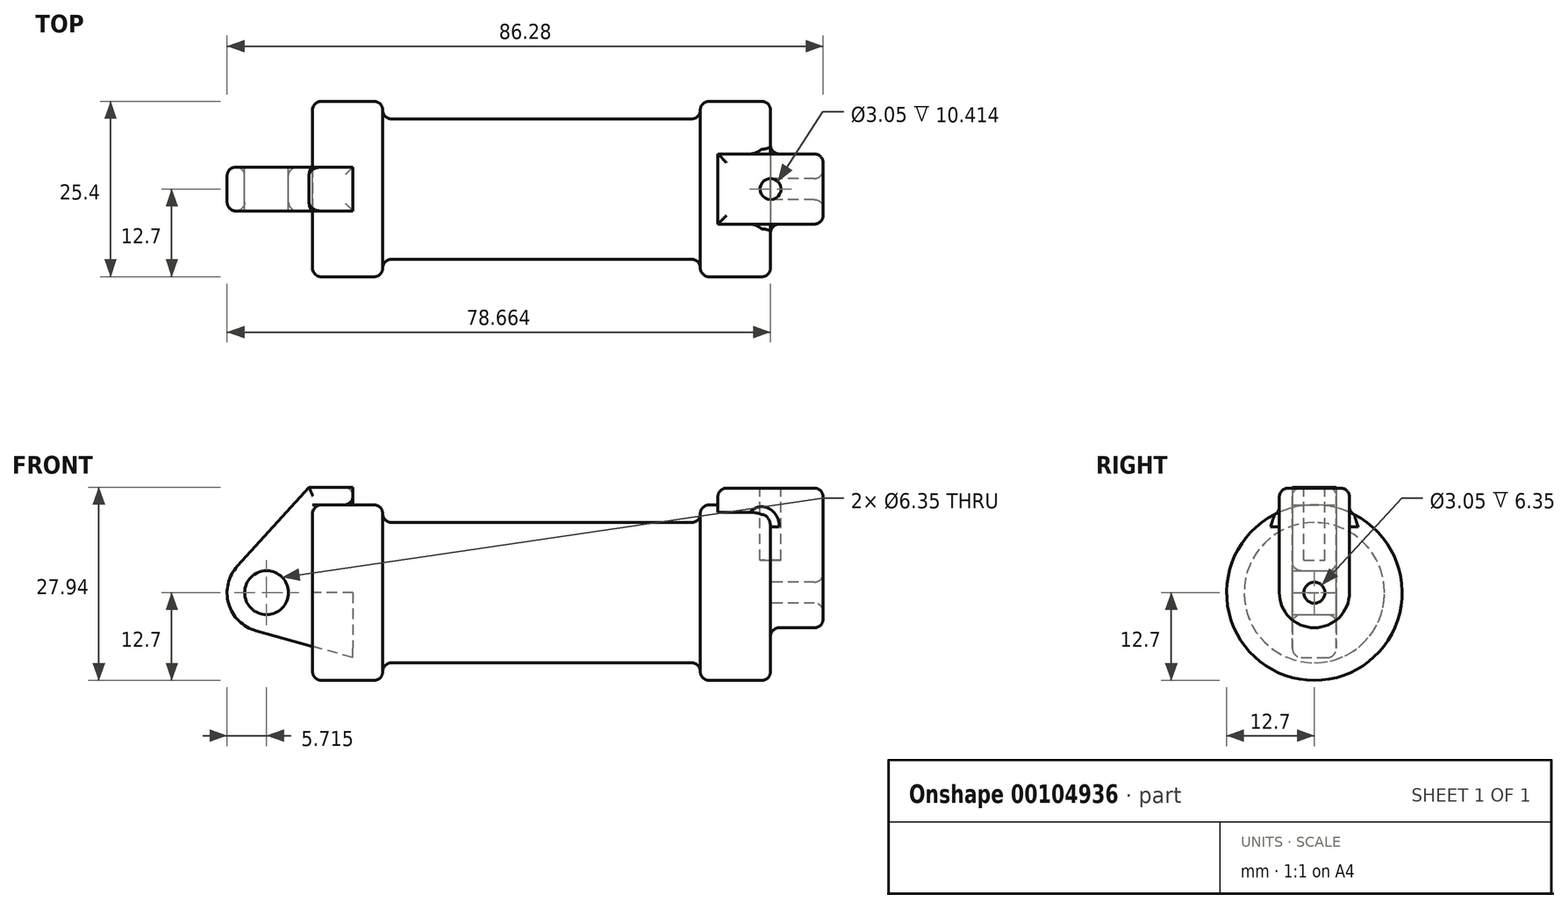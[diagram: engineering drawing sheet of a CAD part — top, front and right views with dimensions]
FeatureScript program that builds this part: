
annotation { "Feature Type Name" : "Feature", "Feature Type Description" : "" }
export const myFeature = defineFeature(function(context is Context, id is Id, definition is map)
    precondition{}
    {
        {
            var Q0;
            Q0=qCreatedBy(makeId("Front.planeOp"),FACE);
            var sketch = newSketch(context, id + "F0", { "sketchPlane" : qUnion([Q0])});
            skLineSegment(sketch, "E0", {"start": v(0, 0) * mm, "end": v(0, 12.7) * mm});
            skLineSegment(sketch, "E1", {"start": v(0, 12.7) * mm, "end": v(10.16, 12.7) * mm});
            skLineSegment(sketch, "E2", {"start": v(10.16, 12.7) * mm, "end": v(10.16, 10.16) * mm});
            skLineSegment(sketch, "E3", {"start": v(10.16, 10.16) * mm, "end": v(56.13, 10.16) * mm});
            skLineSegment(sketch, "E4", {"start": v(56.13, 10.16) * mm, "end": v(56.13, 12.7) * mm});
            skLineSegment(sketch, "E5", {"start": v(56.13, 12.7) * mm, "end": v(66.3, 12.7) * mm});
            skLineSegment(sketch, "E6", {"start": v(66.3, 12.7) * mm, "end": v(66.3, 0) * mm});
            skLineSegment(sketch, "E7", {"start": v(66.3, 0) * mm, "end": v(0, 0) * mm});
            skLineSegment(sketch, "E8", {"start": v(5.84, 15.24) * mm, "end": v(-0.5, 15.24) * mm});
            skLineSegment(sketch, "E9", {"start": v(-0.5, 15.24) * mm, "end": v(-10.88, 3.85) * mm});
            skLineSegment(sketch, "E10", {"start": v(0, 0) * mm, "end": v(-6.65, 0) * mm});
            skCircle(sketch, "E11", {"center": v(-6.65, 0) * mm, "radius": 5.72 * mm});
            skCircle(sketch, "E12", {"center": v(-6.65, 0) * mm, "radius": 3.18 * mm});
            skLineSegment(sketch, "E13", {"start": v(5.84, 15.24) * mm, "end": v(5.84, -9.4) * mm});
            skLineSegment(sketch, "E14", {"start": v(5.84, -9.4) * mm, "end": v(-8.18, -5.5) * mm});
            skSolve(sketch);
        }
        {
            var Q0;
            {var subQ0=sQuery(id+"F0.wireOp",EDGE,"E2");Q0=makeQuery(id+"F0.imprint","IMPRINT",FACE,{"disambiguationData":[TD([[makeQuery(id+"F0.imprint","IMPRINT",EDGE,{"derivedFrom":subQ0}),-1.0]])]});}
            var Q1;
            {var subQ0=sQuery(id+"F0.wireOp",EDGE,"E0");Q1=makeQuery(id+"F0.imprint","IMPRINT",FACE,{"disambiguationData":[TD([[makeQuery(id+"F0.imprint","IMPRINT",EDGE,{"derivedFrom":subQ0}),-1.0]])]});}
            var Q2;
            Q2=sQuery(id+"F0.wireOp",EDGE,"E7");
            revolve(context, id + "F1", {"entities" : qUnion([Q0, Q1]), "axis" : qUnion([Q2]), "revolveType" : RevolveType.FULL});
        }
        {
            var Q0;
            {var subQ3=sQuery(id+"F0.wireOp",EDGE,"E0");Q0=makeQuery(id+"F0.imprint","IMPRINT",FACE,{"disambiguationData":[TD([[makeQuery(id+"F0.imprint","IMPRINT",EDGE,{"derivedFrom":subQ3}),1.0]])]});}
            var Q1;
            {var subQ4=sQuery(id+"F0.wireOp",EDGE,"E12");Q1=makeQuery(id+"F0.imprint","IMPRINT",FACE,{"disambiguationData":[TD([[makeQuery(id+"F0.imprint","IMPRINT",EDGE,{"derivedFrom":subQ4}),-1.0]])]});}
            var Q2;
            {var subQ0=sQuery(id+"F0.wireOp",EDGE,"E14");Q2=makeQuery(id+"F0.imprint","IMPRINT",FACE,{"disambiguationData":[TD([[makeQuery(id+"F0.imprint","IMPRINT",EDGE,{"derivedFrom":subQ0}),-1.0]])]});}
            extrude(context, id + "F2", {"entities" : qUnion([Q0, Q1, Q2]), "endBound" : BoundingType.SYMMETRIC, "depth" : 6.35 * mm, "hasSecondDirection" : true, "secondDirectionOppositeDirection" : true, "secondDirectionDepth" : 25.4 * mm});
        }
        {
            var Q0;
            {var subQ3=sQuery(id+"F0.wireOp",EDGE,"E0");Q0=makeQuery(id+"F0.imprint","IMPRINT",FACE,{"disambiguationData":[TD([[makeQuery(id+"F0.imprint","IMPRINT",EDGE,{"derivedFrom":subQ3}),1.0]])]});}
            var Q1;
            {var subQ0=sQuery(id+"F0.wireOp",EDGE,"E14");Q1=makeQuery(id+"F0.imprint","IMPRINT",FACE,{"disambiguationData":[TD([[makeQuery(id+"F0.imprint","IMPRINT",EDGE,{"derivedFrom":subQ0}),-1.0]])]});}
            var Q2;
            {var subQ4=sQuery(id+"F0.wireOp",EDGE,"E12");Q2=makeQuery(id+"F0.imprint","IMPRINT",FACE,{"disambiguationData":[TD([[makeQuery(id+"F0.imprint","IMPRINT",EDGE,{"derivedFrom":subQ4}),-1.0]])]});}
            extrude(context, id + "F3", {"entities" : qUnion([Q0, Q1, Q2]), "endBound" : BoundingType.SYMMETRIC, "depth" : 6.35 * mm});
        }
        {
            var Q0;
            Q0=makeQuery(id+"F1.opRevolve","SWEPT_FACE",FACE,{"disambiguationData":[OSD([sQuery(id+"F0.wireOp",EDGE,"E6")])]});
            var sketch = newSketch(context, id + "F4", { "sketchPlane" : qUnion([Q0])});
            skCircle(sketch, "E15", {"center": v(0, 0) * mm, "radius": 5.08 * mm});
            skCircle(sketch, "E16", {"center": v(0, 0) * mm, "radius": 1.52 * mm});
            skLineSegment(sketch, "E17", {"start": v(-5.08, 0) * mm, "end": v(-5.08, 15.14) * mm});
            skLineSegment(sketch, "E18", {"start": v(5.08, 0) * mm, "end": v(5.08, 15.14) * mm});
            skLineSegment(sketch, "E19", {"start": v(-5.08, 15.14) * mm, "end": v(5.08, 15.14) * mm});
            skSolve(sketch);
        }
        {
            var Q0;
            {var subQ0=sQuery(id+"F4.wireOp",EDGE,"E17");var subQ1=sQuery(id+"F4.wireOp",EDGE,"E15");var subQ2=makeQuery(id+"F4.imprint","INTERSECT",VERTEX,{"derivedFrom":[subQ1,subQ0]});Q0=makeQuery(id+"F4.imprint","IMPRINT",FACE,{"disambiguationData":[TD([[makeQuery(id+"F4.imprint","IMPRINT",EDGE,{"disambiguationData":[TD([[subQ2,1.0]])],"derivedFrom":subQ1}),-1.0]])]});}
            var Q1;
            Q1=makeQuery(id+"F4.imprint","IMPRINT",FACE,{"disambiguationData":[TD([[makeQuery(id+"F4.imprint","IMPRINT",EDGE,{"derivedFrom":sQuery(id+"F4.wireOp",EDGE,"E16")}),-1.0]])]});
            var Q2;
            {var subQ0=sQuery(id+"F4.wireOp",EDGE,"E19");Q2=makeQuery(id+"F4.imprint","IMPRINT",FACE,{"disambiguationData":[TD([[makeQuery(id+"F4.imprint","IMPRINT",EDGE,{"derivedFrom":subQ0}),-1.0]])]});}
            extrude(context, id + "F5", {"entities" : qUnion([Q0, Q1, Q2]), "operationType" : NewBodyOperationType.ADD, "depth" : 7.62 * mm});
        }
        {
            var Q0;
            Q0=makeQuery(id+"F5.opExtrude","CAP_FACE",FACE,{"disambiguationData":[OSD([sQuery(id+"F4.wireOp",EDGE,"E15"),sQuery(id+"F4.wireOp",EDGE,"E16"),sQuery(id+"F4.wireOp",EDGE,"E17"),sQuery(id+"F4.wireOp",EDGE,"E18"),sQuery(id+"F4.wireOp",EDGE,"E19")])],"isStart":true});
            extrude(context, id + "F6", {"entities" : qUnion([Q0]), "operationType" : NewBodyOperationType.ADD, "depth" : 7.62 * mm, "hasSecondDirection" : true, "secondDirectionOppositeDirection" : true, "secondDirectionDepth" : 1.27 * mm});
        }
        {
            var Q0;
            {var subQ0=sQuery(id+"F4.wireOp",EDGE,"E19");Q0=makeQuery(id+"F6.boolean.opBoolean","MERGE",FACE,{"derivedFrom":[makeQuery(id+"F5.opExtrude","SWEPT_FACE",FACE,{"disambiguationData":[OSD([subQ0])]}),makeQuery(id+"F6.opExtrude","SWEPT_FACE",FACE,{"disambiguationData":[OSD([subQ0])]})]});}
            var sketch = newSketch(context, id + "F7", { "sketchPlane" : qUnion([Q0])});
            skCircle(sketch, "E20", {"center": v(66.3, 0) * mm, "radius": 1.52 * mm});
            skPoint(sketch, "E21.end.orphan", {"position": v(58.67, 0) * mm});
            skPoint(sketch, "E22.orphan", {"position": v(73.91, 0) * mm});
            skPoint(sketch, "E23.start.orphan", {"position": v(66.3, -5.08) * mm});
            skPoint(sketch, "E24.trimOffspring.end.orphan", {"position": v(66.3, 5.08) * mm});
            skSolve(sketch);
        }
        {
            var Q0;
            Q0=makeQuery(id+"F7.imprint","IMPRINT",FACE,{"disambiguationData":[TD([[makeQuery(id+"F7.imprint","IMPRINT",EDGE,{"derivedFrom":sQuery(id+"F7.wireOp",EDGE,"E20")}),1.0]])]});
            extrude(context, id + "F8", {"entities" : qUnion([Q0]), "operationType" : NewBodyOperationType.REMOVE, "oppositeDirection" : true, "depth" : 10.4 * mm});
        }
        {
            var Q0;
            Q0=makeQuery(id+"F2.opExtrude","SWEPT_EDGE",EDGE,{"disambiguationData":[OSD([sQuery(id+"F0.wireOp",EDGE,"E8"),sQuery(id+"F0.wireOp",EDGE,"E13")])]});
            var Q1;
            Q1=makeQuery(id+"F2.opExtrude","CAP_EDGE",EDGE,{"disambiguationData":[OSD([sQuery(id+"F0.wireOp",EDGE,"E9")])],"isStart":false});
            var Q2;
            Q2=makeQuery(id+"FKCR7nvXK0qdjoD_2.boolean.opBoolean","COPY",EDGE,{"disambiguationData":[OD(1.0)],"derivedFrom":makeQuery(id+"FKCR7nvXK0qdjoD_2.opExtrude","CAP_EDGE",EDGE,{"disambiguationData":[OSD([sQuery(id+"FypJyNtqC55bvcD_2.wireOp",EDGE,"d1c0e7b1-a245-40cd-82fb-4ff1a312aeeb")])],"isStart":true})});
            var Q3;
            Q3=makeQuery(id+"F3.opExtrude","CAP_EDGE",EDGE,{"disambiguationData":[OSD([sQuery(id+"F0.wireOp",EDGE,"E11")])],"isStart":false});
            var Q4;
            Q4=makeQuery(id+"F2.opExtrude","CAP_EDGE",EDGE,{"disambiguationData":[OSD([sQuery(id+"F0.wireOp",EDGE,"E14")])],"isStart":false});
            var Q5;
            Q5=makeQuery(id+"F2.opExtrude","CAP_EDGE",EDGE,{"disambiguationData":[OSD([sQuery(id+"F0.wireOp",EDGE,"E14")])],"isStart":true});
            var Q6;
            Q6=makeQuery(id+"F3.opExtrude","CAP_EDGE",EDGE,{"disambiguationData":[OSD([sQuery(id+"F0.wireOp",EDGE,"E11")])],"isStart":true});
            var Q7;
            Q7=makeQuery(id+"F2.opExtrude","CAP_EDGE",EDGE,{"disambiguationData":[OSD([sQuery(id+"F0.wireOp",EDGE,"E9")])],"isStart":true});
            var Q8;
            Q8=makeQuery(id+"F3.opExtrude","CAP_EDGE",EDGE,{"disambiguationData":[OSD([sQuery(id+"F0.wireOp",EDGE,"E12")])],"isStart":true});
            var Q9;
            Q9=makeQuery(id+"F1.opRevolve","SWEPT_EDGE",EDGE,{"disambiguationData":[OSD([sQuery(id+"F0.wireOp",EDGE,"E0"),sQuery(id+"F0.wireOp",EDGE,"E1")])]});
            var Q10;
            Q10=makeQuery(id+"F1.opRevolve","SWEPT_EDGE",EDGE,{"disambiguationData":[OSD([sQuery(id+"F0.wireOp",EDGE,"E1"),sQuery(id+"F0.wireOp",EDGE,"E2")])]});
            var Q11;
            Q11=makeQuery(id+"F2.opExtrude","CAP_EDGE",EDGE,{"disambiguationData":[OSD([sQuery(id+"F0.wireOp",EDGE,"E8")])],"isStart":false});
            var Q12;
            Q12=makeQuery(id+"F2.opExtrude","CAP_EDGE",EDGE,{"disambiguationData":[OSD([sQuery(id+"F0.wireOp",EDGE,"E8")])],"isStart":true});
            var Q13;
            Q13=makeQuery(id+"F2.opExtrude","SWEPT_EDGE",EDGE,{"disambiguationData":[OSD([sQuery(id+"F0.wireOp",EDGE,"E1"),sQuery(id+"F0.wireOp",EDGE,"E13")])]});
            var Q14;
            Q14=makeQuery(id+"F5.opExtrude","CAP_EDGE",EDGE,{"disambiguationData":[OSD([sQuery(id+"F4.wireOp",EDGE,"E18")])],"isStart":false});
            var Q15;
            Q15=makeQuery(id+"F5.opExtrude","CAP_EDGE",EDGE,{"disambiguationData":[OSD([sQuery(id+"F4.wireOp",EDGE,"E15")])],"isStart":false});
            var Q16;
            Q16=makeQuery(id+"F5.boolean.opBoolean","SPLIT",EDGE,{"disambiguationData":[OD(1.0)],"derivedFrom":makeQuery(id+"F1.opRevolve","SWEPT_EDGE",EDGE,{"disambiguationData":[OSD([sQuery(id+"F0.wireOp",EDGE,"E5"),sQuery(id+"F0.wireOp",EDGE,"E6")])]})});
            var Q17;
            Q17=makeQuery(id+"F1.opRevolve","SWEPT_EDGE",EDGE,{"disambiguationData":[OSD([sQuery(id+"F0.wireOp",EDGE,"E4"),sQuery(id+"F0.wireOp",EDGE,"E5")])]});
            var Q18;
            Q18=makeQuery(id+"F1.opRevolve","SWEPT_EDGE",EDGE,{"disambiguationData":[OSD([sQuery(id+"F0.wireOp",EDGE,"E3"),sQuery(id+"F0.wireOp",EDGE,"E4")])]});
            var Q19;
            {var subQ0=sQuery(id+"F4.wireOp",EDGE,"E19");var subQ1=sQuery(id+"F4.wireOp",EDGE,"E17");Q19=makeQuery(id+"F6.boolean.opBoolean","MERGE",EDGE,{"derivedFrom":[makeQuery(id+"F5.opExtrude","SWEPT_EDGE",EDGE,{"disambiguationData":[OSD([subQ1,subQ0])]}),makeQuery(id+"F6.opExtrude","SWEPT_EDGE",EDGE,{"disambiguationData":[OSD([subQ1,subQ0])]})]});}
            var Q20;
            Q20=makeQuery(id+"F5.opExtrude","CAP_EDGE",EDGE,{"disambiguationData":[OSD([sQuery(id+"F4.wireOp",EDGE,"E19")])],"isStart":false});
            var Q21;
            {var subQ0=sQuery(id+"F4.wireOp",EDGE,"E19");var subQ1=sQuery(id+"F4.wireOp",EDGE,"E18");Q21=makeQuery(id+"F6.boolean.opBoolean","MERGE",EDGE,{"derivedFrom":[makeQuery(id+"F5.opExtrude","SWEPT_EDGE",EDGE,{"disambiguationData":[OSD([subQ1,subQ0])]}),makeQuery(id+"F6.opExtrude","SWEPT_EDGE",EDGE,{"disambiguationData":[OSD([subQ1,subQ0])]})]});}
            var Q22;
            Q22=makeQuery(id+"F5.opExtrude","CAP_EDGE",EDGE,{"disambiguationData":[OSD([sQuery(id+"F4.wireOp",EDGE,"E16")])],"isStart":false});
            var Q23;
            Q23=makeQuery(id+"F6.opExtrude","CAP_EDGE",EDGE,{"disambiguationData":[OSD([sQuery(id+"F4.wireOp",EDGE,"E19")])],"isStart":false});
            var Q24;
            Q24=makeQuery(id+"F8.boolean.opBoolean","COPY",EDGE,{"derivedFrom":makeQuery(id+"F8.opExtrude","CAP_EDGE",EDGE,{"disambiguationData":[OSD([sQuery(id+"F7.wireOp",EDGE,"E20")])],"isStart":true})});
            var Q25;
            Q25=makeQuery(id+"F3.opExtrude","CAP_EDGE",EDGE,{"disambiguationData":[OSD([sQuery(id+"F0.wireOp",EDGE,"E12")])],"isStart":false});
            var Q26;
            Q26=makeQuery(id+"F1.opRevolve","SWEPT_EDGE",EDGE,{"disambiguationData":[OSD([sQuery(id+"F0.wireOp",EDGE,"E2"),sQuery(id+"F0.wireOp",EDGE,"E3")])]});
            var Q27;
            Q27=makeQuery(id+"F5.opExtrude","CAP_EDGE",EDGE,{"disambiguationData":[OSD([sQuery(id+"F4.wireOp",EDGE,"E15")])],"isStart":true});
            var Q28;
            {var subQ0=sQuery(id+"F4.wireOp",EDGE,"E17");var subQ1=sQuery(id+"F4.wireOp",EDGE,"E19");var subQ2=sQuery(id+"F4.wireOp",EDGE,"E18");var subQ3=sQuery(id+"F4.wireOp",EDGE,"E16");var subQ4=sQuery(id+"F4.wireOp",EDGE,"E15");var subQ5=sQuery(id+"F0.wireOp",EDGE,"E6");var subQ6=sQuery(id+"F0.wireOp",EDGE,"E5");Q28=makeQuery(id+"F6.opExtrude","SWEPT_EDGE",EDGE,{"disambiguationData":[OSD([subQ6,subQ5,subQ4,subQ3,subQ0,subQ2,subQ1]),TDD([makeQuery(id+"F5.boolean.opBoolean","TWEAK_VERTEX",VERTEX,{"derivedFrom":[makeQuery(id+"F1.opRevolve","SWEPT_FACE",FACE,{"disambiguationData":[OSD([subQ6])]}),makeQuery(id+"F1.opRevolve","SWEPT_FACE",FACE,{"disambiguationData":[OSD([subQ5])]}),makeQuery(id+"F5.opExtrude","CAP_FACE",FACE,{"disambiguationData":[OSD([subQ4,subQ3,subQ0,subQ2,subQ1])],"isStart":true}),makeQuery(id+"F5.opExtrude","SWEPT_FACE",FACE,{"disambiguationData":[OSD([subQ0])]})]})])]});}
            var Q29;
            {var subQ0=sQuery(id+"F4.wireOp",EDGE,"E17");var subQ1=sQuery(id+"F4.wireOp",EDGE,"E15");Q29=makeQuery(id+"F5.boolean.opBoolean","SPLIT",EDGE,{"disambiguationData":[TD([makeQuery(id+"F5.opExtrude","SWEPT_FACE",FACE,{"disambiguationData":[OSD([subQ1])]})])],"derivedFrom":makeQuery(id+"F5.opExtrude","CAP_EDGE",EDGE,{"disambiguationData":[OSD([subQ0])],"isStart":true})});}
            var Q30;
            {var subQ0=sQuery(id+"F4.wireOp",EDGE,"E18");var subQ1=sQuery(id+"F4.wireOp",EDGE,"E15");Q30=makeQuery(id+"F5.boolean.opBoolean","SPLIT",EDGE,{"disambiguationData":[TD([makeQuery(id+"F5.opExtrude","SWEPT_FACE",FACE,{"disambiguationData":[OSD([subQ1])]})])],"derivedFrom":makeQuery(id+"F5.opExtrude","CAP_EDGE",EDGE,{"disambiguationData":[OSD([subQ0])],"isStart":true})});}
            var Q31;
            {var subQ0=sQuery(id+"F4.wireOp",EDGE,"E18");var subQ1=sQuery(id+"F4.wireOp",EDGE,"E19");var subQ2=sQuery(id+"F4.wireOp",EDGE,"E17");var subQ3=sQuery(id+"F4.wireOp",EDGE,"E16");var subQ4=sQuery(id+"F4.wireOp",EDGE,"E15");var subQ5=sQuery(id+"F0.wireOp",EDGE,"E6");var subQ6=sQuery(id+"F0.wireOp",EDGE,"E5");Q31=makeQuery(id+"F6.opExtrude","SWEPT_EDGE",EDGE,{"disambiguationData":[OSD([subQ6,subQ5,subQ4,subQ3,subQ2,subQ0,subQ1]),TDD([makeQuery(id+"F5.boolean.opBoolean","TWEAK_VERTEX",VERTEX,{"derivedFrom":[makeQuery(id+"F1.opRevolve","SWEPT_FACE",FACE,{"disambiguationData":[OSD([subQ6])]}),makeQuery(id+"F1.opRevolve","SWEPT_FACE",FACE,{"disambiguationData":[OSD([subQ5])]}),makeQuery(id+"F5.opExtrude","CAP_FACE",FACE,{"disambiguationData":[OSD([subQ4,subQ3,subQ2,subQ0,subQ1])],"isStart":true}),makeQuery(id+"F5.opExtrude","SWEPT_FACE",FACE,{"disambiguationData":[OSD([subQ0])]})]})])]});}
            fillet(context, id + "F9", {"entities" : qUnion([Q0, Q1, Q2, Q3, Q4, Q5, Q6, Q7, Q8, Q9, Q10, Q11, Q12, Q13, Q14, Q15, Q16, Q17, Q18, Q19, Q20, Q21, Q22, Q23, Q24, Q25, Q26, Q27, Q28, Q29, Q30, Q31]), "radius" : 1.27 * mm, "tangentPropagation" : true, "allowEdgeOverflow" : false});
        }
    });
